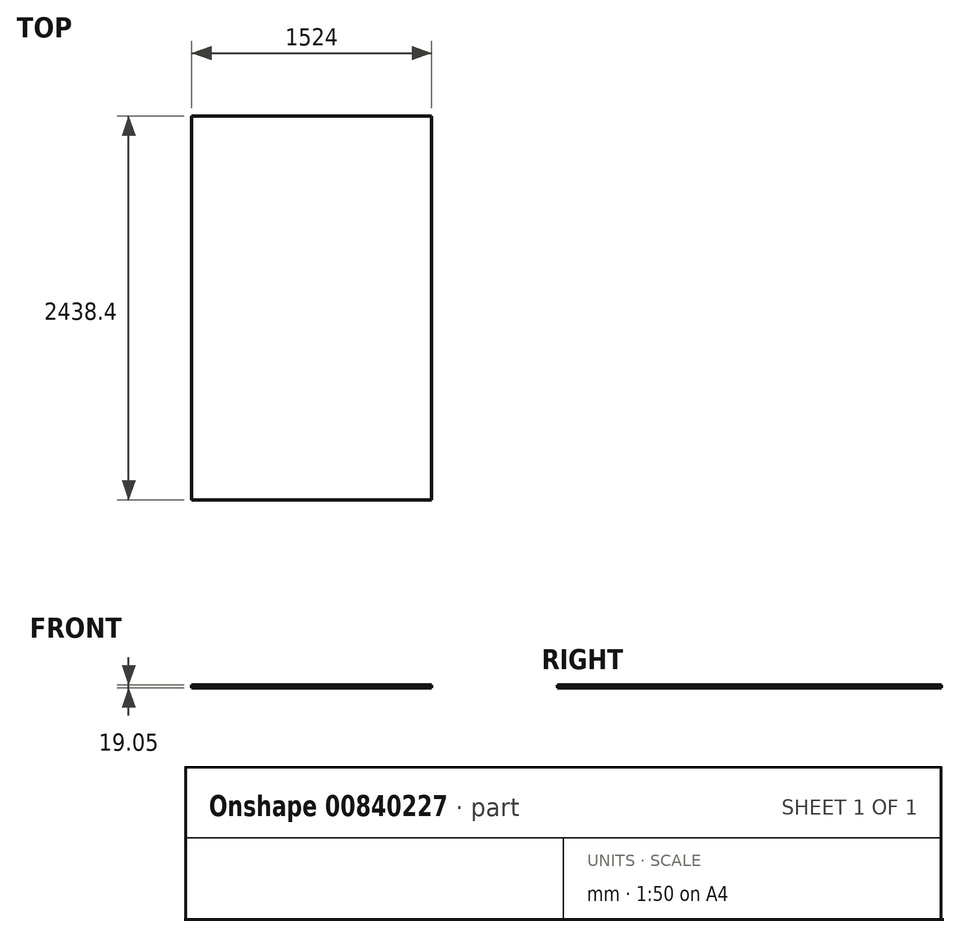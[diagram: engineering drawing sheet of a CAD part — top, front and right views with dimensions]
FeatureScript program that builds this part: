
annotation { "Feature Type Name" : "Feature", "Feature Type Description" : "" }
export const myFeature = defineFeature(function(context is Context, id is Id, definition is map)
    precondition{}
    {
        {
            var Q0;
            Q0=qCreatedBy(makeId("Top.planeOp"),FACE);
            var sketch = newSketch(context, id + "F0", { "sketchPlane" : qUnion([Q0])});
            skLineSegment(sketch, "E0.bottom", {"start": v(0, 0) * mm, "end": v(1524, 0) * mm});
            skLineSegment(sketch, "E0.top", {"start": v(0, 2438.4) * mm, "end": v(1524, 2438.4) * mm});
            skLineSegment(sketch, "E0.left", {"start": v(0, 0) * mm, "end": v(0, 2438.4) * mm});
            skLineSegment(sketch, "E0.right", {"start": v(1524, 0) * mm, "end": v(1524, 2438.4) * mm});
            skSolve(sketch);
        }
        {
            var Q0;
            Q0 = qSketchRegion(id + "F0", true);
            extrude(context, id + "F1", {"entities" : qUnion([Q0]), "depth" : 19.05 * mm, "offsetDistance" : 25.4 * mm});
        }
    });
